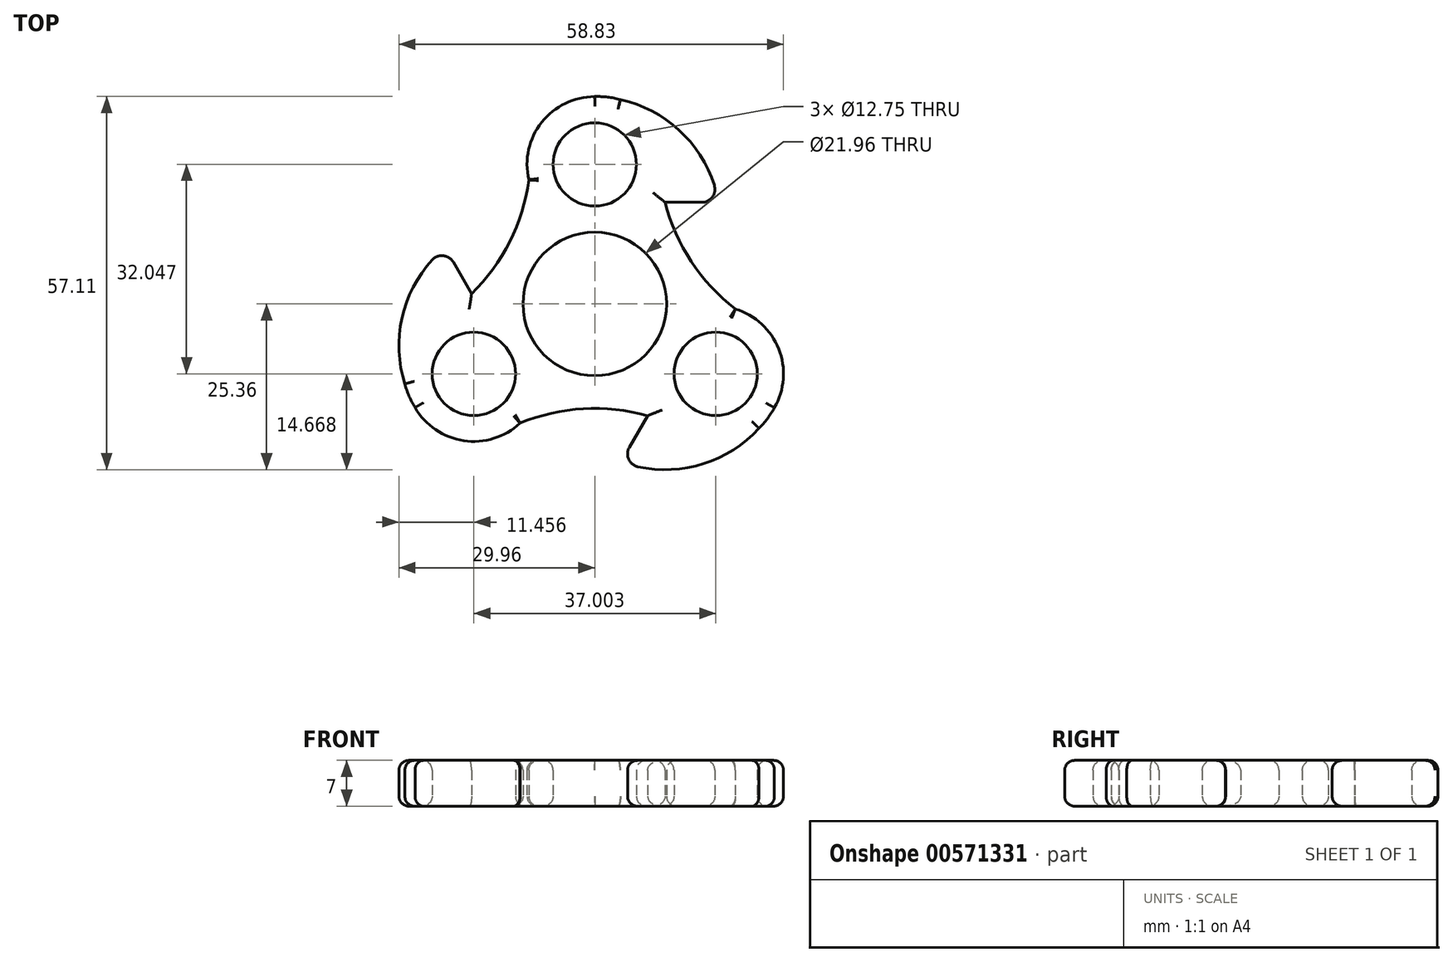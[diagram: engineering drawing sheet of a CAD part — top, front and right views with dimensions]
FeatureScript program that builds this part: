
annotation { "Feature Type Name" : "Feature", "Feature Type Description" : "" }
export const myFeature = defineFeature(function(context is Context, id is Id, definition is map)
    precondition{}
    {
        {
            var Q0;
            Q0=qCreatedBy(makeId("Top.planeOp"),FACE);
            var sketch = newSketch(context, id + "F0", { "sketchPlane" : qUnion([Q0])});
            skCircle(sketch, "E0", {"center": v(0, 0) * mm, "radius": 10.98 * mm});
            skCircle(sketch, "E1", {"center": v(0, 21.35) * mm, "radius": 6.38 * mm});
            skCircle(sketch, "E2.1.0", {"center": v(-18.5, -10.69) * mm, "radius": 6.38 * mm});
            skCircle(sketch, "E2.2.0", {"center": v(18.5, -10.7) * mm, "radius": 6.38 * mm});
            skArc(sketch, "E3.1.0", {"start": v(-0.03, 10.98) * mm, "mid": v(0.02, 10.98) * mm, "end": v(0.06, 10.98) * mm});
            skPoint(sketch, "E3.center", {"position": v(0.01, 0) * mm});
            skLineSegment(sketch, "E4.2.0", {"start": v(-21.47, -0.73) * mm, "end": v(-21.47, -0.73) * mm});
            skArc(sketch, "E5", {"start": v(10.77, 15.55) * mm, "mid": v(14.76, 6.5) * mm, "end": v(21.49, -0.76) * mm});
            skArc(sketch, "E6.trimOffspring", {"start": v(-9.33, -5.8) * mm, "mid": v(-9.5, -5.48) * mm, "end": v(-9.69, -5.17) * mm});
            skArc(sketch, "E7.1.1", {"start": v(0, 31.74) * mm, "mid": v(-8.11, 27.82) * mm, "end": v(-10.09, 19.02) * mm});
            skArc(sketch, "E8", {"start": v(3.91, 31.28) * mm, "mid": v(1.98, 31.65) * mm, "end": v(0, 31.74) * mm});
            skArc(sketch, "E9", {"start": v(10.11, 18.98) * mm, "mid": v(10.1, 18.97) * mm, "end": v(10.1, 18.96) * mm});
            skArc(sketch, "E10.1.1", {"start": v(-27.5, -15.86) * mm, "mid": v(-20.05, -20.93) * mm, "end": v(-11.45, -18.27) * mm});
            skArc(sketch, "E10.1.2", {"start": v(-18.85, 1.55) * mm, "mid": v(-13.01, 9.54) * mm, "end": v(-10.09, 18.99) * mm});
            skArc(sketch, "E10.1.3", {"start": v(-21.49, -0.73) * mm, "mid": v(-21.48, -0.73) * mm, "end": v(-21.47, -0.73) * mm});
            skArc(sketch, "E10.2.1", {"start": v(27.48, -15.88) * mm, "mid": v(28.15, -6.89) * mm, "end": v(21.52, -0.77) * mm});
            skArc(sketch, "E10.2.2", {"start": v(8.09, -17.1) * mm, "mid": v(-1.75, -16.04) * mm, "end": v(-11.4, -18.23) * mm});
            skArc(sketch, "E10.2.3", {"start": v(11.38, -18.25) * mm, "mid": v(11.38, -18.24) * mm, "end": v(11.37, -18.23) * mm});
            skLineSegment(sketch, "E11", {"start": v(21.49, -0.76) * mm, "end": v(21.52, -0.77) * mm});
            skLineSegment(sketch, "E12", {"start": v(-11.4, -18.23) * mm, "end": v(-11.45, -18.27) * mm});
            skLineSegment(sketch, "E13", {"start": v(-10.09, 18.99) * mm, "end": v(-10.09, 19.02) * mm});
            skPoint(sketch, "E14.orphan", {"position": v(-10.08, 18.99) * mm});
            skArc(sketch, "E15", {"start": v(18.92, 15.55) * mm, "mid": v(13.81, 25.7) * mm, "end": v(3.91, 31.28) * mm});
            skLineSegment(sketch, "E16", {"start": v(18.92, 15.55) * mm, "end": v(10.77, 15.55) * mm});
            skLineSegment(sketch, "E17.1.0", {"start": v(-22.93, 8.6) * mm, "end": v(-18.85, 1.55) * mm});
            skArc(sketch, "E17.1.1", {"start": v(-22.93, 8.6) * mm, "mid": v(-29.17, -0.9) * mm, "end": v(-29.05, -12.25) * mm});
            skArc(sketch, "E17.1.2", {"start": v(-29.05, -12.25) * mm, "mid": v(-28.4, -14.11) * mm, "end": v(-27.5, -15.86) * mm});
            skLineSegment(sketch, "E17.2.0", {"start": v(4.01, -24.16) * mm, "end": v(8.09, -17.1) * mm});
            skArc(sketch, "E17.2.1", {"start": v(4.01, -24.16) * mm, "mid": v(15.36, -24.82) * mm, "end": v(25.14, -19.03) * mm});
            skArc(sketch, "E17.2.2", {"start": v(25.14, -19.03) * mm, "mid": v(26.42, -17.54) * mm, "end": v(27.48, -15.88) * mm});
            skSolve(sketch);
        }
        {
            var Q0;
            Q0=qSketchRegion(id+"F0",true);
            extrude(context, id + "F1", {"entities" : qUnion([Q0]), "depth" : 7 * mm, "offsetDistance" : 25 * mm});
        }
        {
            var Q0;
            Q0=makeQuery(id+"F1.opExtrude","CAP_FACE",FACE,{"disambiguationData":[OSD([sQuery(id+"F0.wireOp",EDGE,"E0"),sQuery(id+"F0.wireOp",EDGE,"E1"),sQuery(id+"F0.wireOp",EDGE,"E2.1.0"),sQuery(id+"F0.wireOp",EDGE,"E2.2.0"),sQuery(id+"F0.wireOp",EDGE,"AXVinLNo-2nWp-v7ZV-fhIw-7YEQeObZwanW"),sQuery(id+"F0.wireOp",EDGE,"E5"),sQuery(id+"F0.wireOp",EDGE,"E7.1.0"),sQuery(id+"F0.wireOp",EDGE,"E7.1.1"),sQuery(id+"F0.wireOp",EDGE,"E7.2.0"),sQuery(id+"F0.wireOp",EDGE,"E7.2.1")])],"isStart":false});
            var Q1;
            Q1=makeQuery(id+"F1.opExtrude","CAP_FACE",FACE,{"disambiguationData":[OSD([sQuery(id+"F0.wireOp",EDGE,"E0"),sQuery(id+"F0.wireOp",EDGE,"E1"),sQuery(id+"F0.wireOp",EDGE,"E2.1.0"),sQuery(id+"F0.wireOp",EDGE,"E2.2.0"),sQuery(id+"F0.wireOp",EDGE,"AXVinLNo-2nWp-v7ZV-fhIw-7YEQeObZwanW"),sQuery(id+"F0.wireOp",EDGE,"E5"),sQuery(id+"F0.wireOp",EDGE,"E7.1.0"),sQuery(id+"F0.wireOp",EDGE,"E7.1.1"),sQuery(id+"F0.wireOp",EDGE,"E7.2.0"),sQuery(id+"F0.wireOp",EDGE,"E7.2.1")])],"isStart":true});
            fillet(context, id + "F2", {"entities" : qUnion([Q0, Q1]), "radius" : 1.5 * mm, "tangentPropagation" : true, "allowEdgeOverflow" : false});
        }
        {
            var Q0;
            Q0=makeQuery(id+"F1.opExtrude","SWEPT_EDGE",EDGE,{"disambiguationData":[OSD([sQuery(id+"F0.wireOp",EDGE,"E8"),sQuery(id+"F0.wireOp",EDGE,"ikTaHUG2-97tr-M9zG-rNM4-ONcQalVcCPlP")])]});
            var Q1;
            Q1=makeQuery(id+"F1.opExtrude","SWEPT_EDGE",EDGE,{"disambiguationData":[OSD([sQuery(id+"F0.wireOp",EDGE,"E10.2.0"),sQuery(id+"F0.wireOp",EDGE,"E10.2.4")])]});
            var Q2;
            Q2=makeQuery(id+"F1.opExtrude","SWEPT_EDGE",EDGE,{"disambiguationData":[OSD([sQuery(id+"F0.wireOp",EDGE,"E10.1.0"),sQuery(id+"F0.wireOp",EDGE,"E10.1.4")])]});
            var Q3;
            Q3=makeQuery(id+"F1.opExtrude","SWEPT_EDGE",EDGE,{"disambiguationData":[OSD([sQuery(id+"F0.wireOp",EDGE,"E17.1.0"),sQuery(id+"F0.wireOp",EDGE,"E17.1.1")])]});
            var Q4;
            Q4=makeQuery(id+"F1.opExtrude","SWEPT_EDGE",EDGE,{"disambiguationData":[OSD([sQuery(id+"F0.wireOp",EDGE,"E15"),sQuery(id+"F0.wireOp",EDGE,"E16")])]});
            var Q5;
            Q5=makeQuery(id+"F1.opExtrude","SWEPT_EDGE",EDGE,{"disambiguationData":[OSD([sQuery(id+"F0.wireOp",EDGE,"E17.2.0"),sQuery(id+"F0.wireOp",EDGE,"E17.2.1")])]});
            fillet(context, id + "F3", {"entities" : qUnion([Q0, Q1, Q2, Q3, Q4, Q5]), "radius" : 2 * mm, "tangentPropagation" : true, "allowEdgeOverflow" : false});
        }
    });
